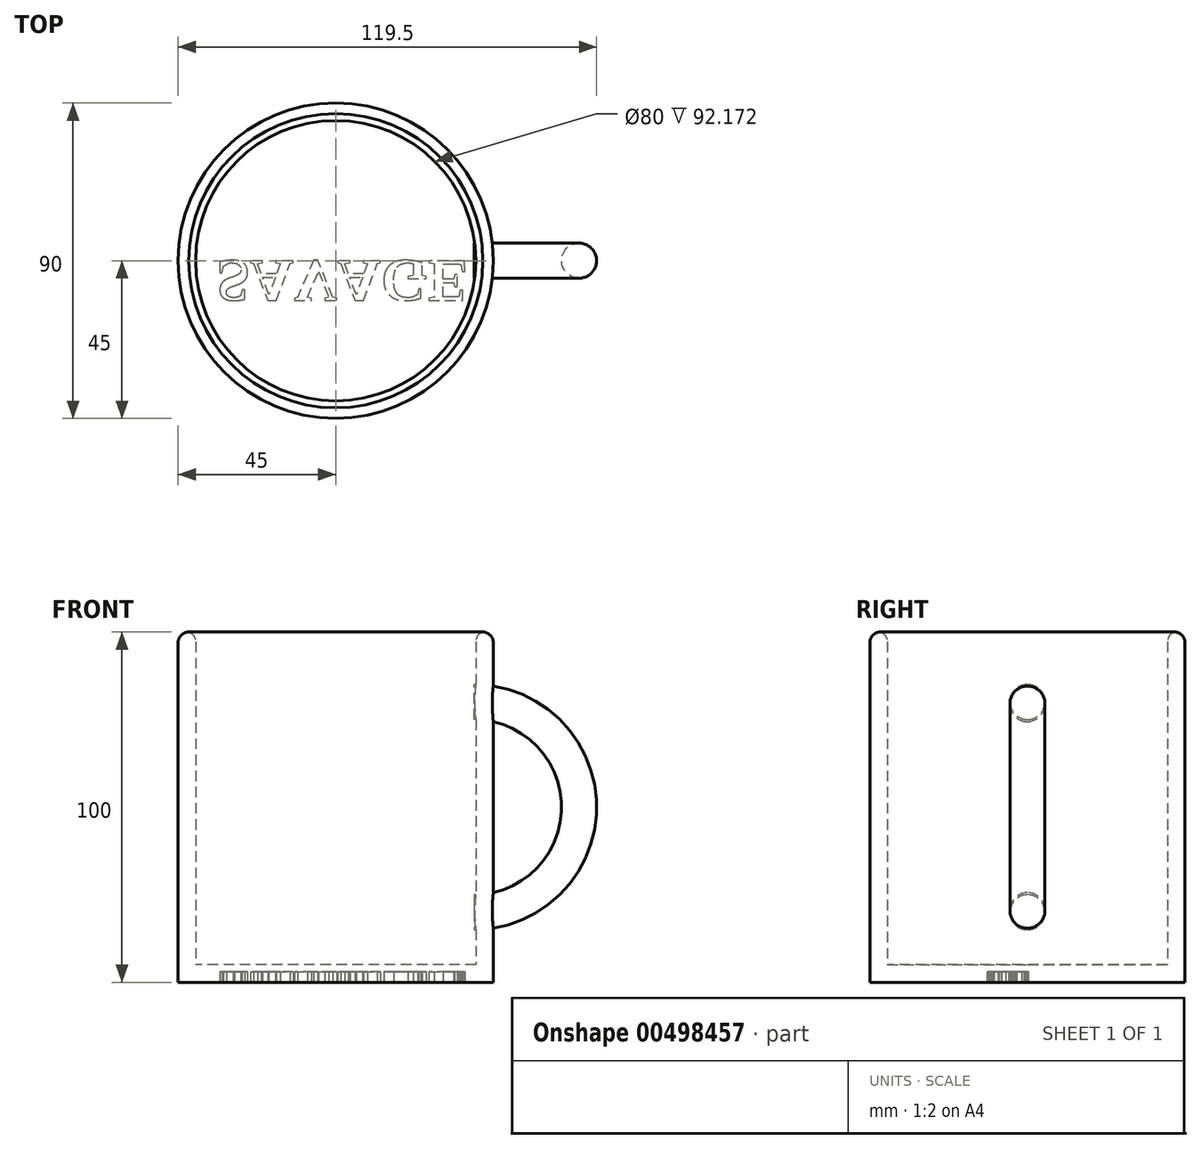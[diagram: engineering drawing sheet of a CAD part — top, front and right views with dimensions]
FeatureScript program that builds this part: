
annotation { "Feature Type Name" : "Feature", "Feature Type Description" : "" }
export const myFeature = defineFeature(function(context is Context, id is Id, definition is map)
    precondition{}
    {
        {
            var Q0;
            Q0=qCreatedBy(makeId("Top.planeOp"),FACE);
            var sketch = newSketch(context, id + "F0", { "sketchPlane" : qUnion([Q0])});
            skCircle(sketch, "E0", {"center": v(0, 0) * mm, "radius": 45 * mm});
            skSolve(sketch);
        }
        {
            var Q0;
            Q0 = qSketchRegion(id + "F0", true);
            extrude(context, id + "F1", {"entities" : qUnion([Q0]), "depth" : 100 * mm});
        }
        {
            var Q0;
            Q0=makeQuery(id+"F1.opExtrude","CAP_FACE",FACE,{"disambiguationData":[OSD([sQuery(id+"F0.wireOp",EDGE,"E0")])],"isStart":false});
            shell(context, id + "F2", {"entities" : qUnion([Q0]), "thickness" : 5 * mm});
        }
        {
            var Q0;
            Q0=qCreatedBy(makeId("Right.planeOp"),FACE);
            cPlane(context, id + "F3", {"entities" : qUnion([Q0]), "cplaneType" : CPlaneType.OFFSET, "offset" : 39.5 * mm, "width" : 150 * mm, "height" : 150 * mm});
        }
        {
            var Q0;
            Q0=qCreatedBy(id+"F3.planeOp",FACE);
            var sketch = newSketch(context, id + "F4", { "sketchPlane" : qUnion([Q0])});
            skCircle(sketch, "E1", {"center": v(0, 80) * mm, "radius": 5 * mm});
            skLineSegment(sketch, "E2", {"start": v(0, 50) * mm, "end": v(26.37, 50) * mm});
            skSolve(sketch);
        }
        {
            var Q0;
            Q0 = qSketchRegion(id + "F4", true);
            var Q1;
            Q1=sQuery(id+"F4.wireOp",EDGE,"E2");
            revolve(context, id + "F5", {"operationType" : NewBodyOperationType.ADD, "entities" : qUnion([Q0]), "axis" : qUnion([Q1]), "revolveType" : RevolveType.ONE_DIRECTION, "angle" : 180 * degree});
        }
        {
            var Q0;
            Q0=makeQuery(id+"F1.opExtrude","CAP_EDGE",EDGE,{"disambiguationData":[OSD([sQuery(id+"F0.wireOp",EDGE,"E0")])],"isStart":false});
            fillet(context, id + "F6", {"entities" : qUnion([Q0]), "radius" : 3 * mm, "tangentPropagation" : true, "allowEdgeOverflow" : false});
        }
        {
            var Q0;
            {var subQ0=sQuery(id+"F0.wireOp",EDGE,"E0");Q0=makeQuery(id+"F6.opFillet","BLEND_EDGE",EDGE,{"blendedFrom":[makeQuery(id+"F1.opExtrude","CAP_EDGE",EDGE,{"disambiguationData":[OSD([subQ0])],"isStart":false}),makeQuery(id+"F1.opExtrude","CAP_FACE",FACE,{"disambiguationData":[OSD([subQ0])],"isStart":false})],"blendedInto":[makeQuery(id+"F1.opExtrude","CAP_FACE",FACE,{"disambiguationData":[OSD([subQ0])],"isStart":false})]});}
            var Q1;
            {var subQ0=sQuery(id+"F0.wireOp",EDGE,"E0");Q1=makeQuery(id+"F2.opShell","OFFSET_EDGE",EDGE,{"disambiguationData":[OSD([subQ0]),TDD([makeQuery(id+"F1.opExtrude","CAP_EDGE",EDGE,{"disambiguationData":[OSD([subQ0])],"isStart":false})])]});}
            fillet(context, id + "F7", {"entities" : qUnion([Q0, Q1]), "radius" : 3 * mm, "tangentPropagation" : true, "allowEdgeOverflow" : false});
        }
        {
            var Q0;
            Q0=makeQuery(id+"F1.opExtrude","CAP_FACE",FACE,{"disambiguationData":[OSD([sQuery(id+"F0.wireOp",EDGE,"E0")])],"isStart":true});
            var sketch = newSketch(context, id + "F8", { "sketchPlane" : qUnion([Q0])});
            skText(sketch, "E3", { "text": "SAVAGE", "fontName": "Tinos-Bold.ttf"});
            const initialGuessF8  = {"E3": [-0.03406, 0, 1, 0, 0.01242]};
            skSetInitialGuess(sketch, initialGuessF8);
            skSolve(sketch);
        }
        {
            var Q0;
            Q0 = qSketchRegion(id + "F8", true);
            extrude(context, id + "F9", {"entities" : qUnion([Q0]), "operationType" : NewBodyOperationType.REMOVE, "oppositeDirection" : true, "depth" : 3 * mm});
        }
    });
